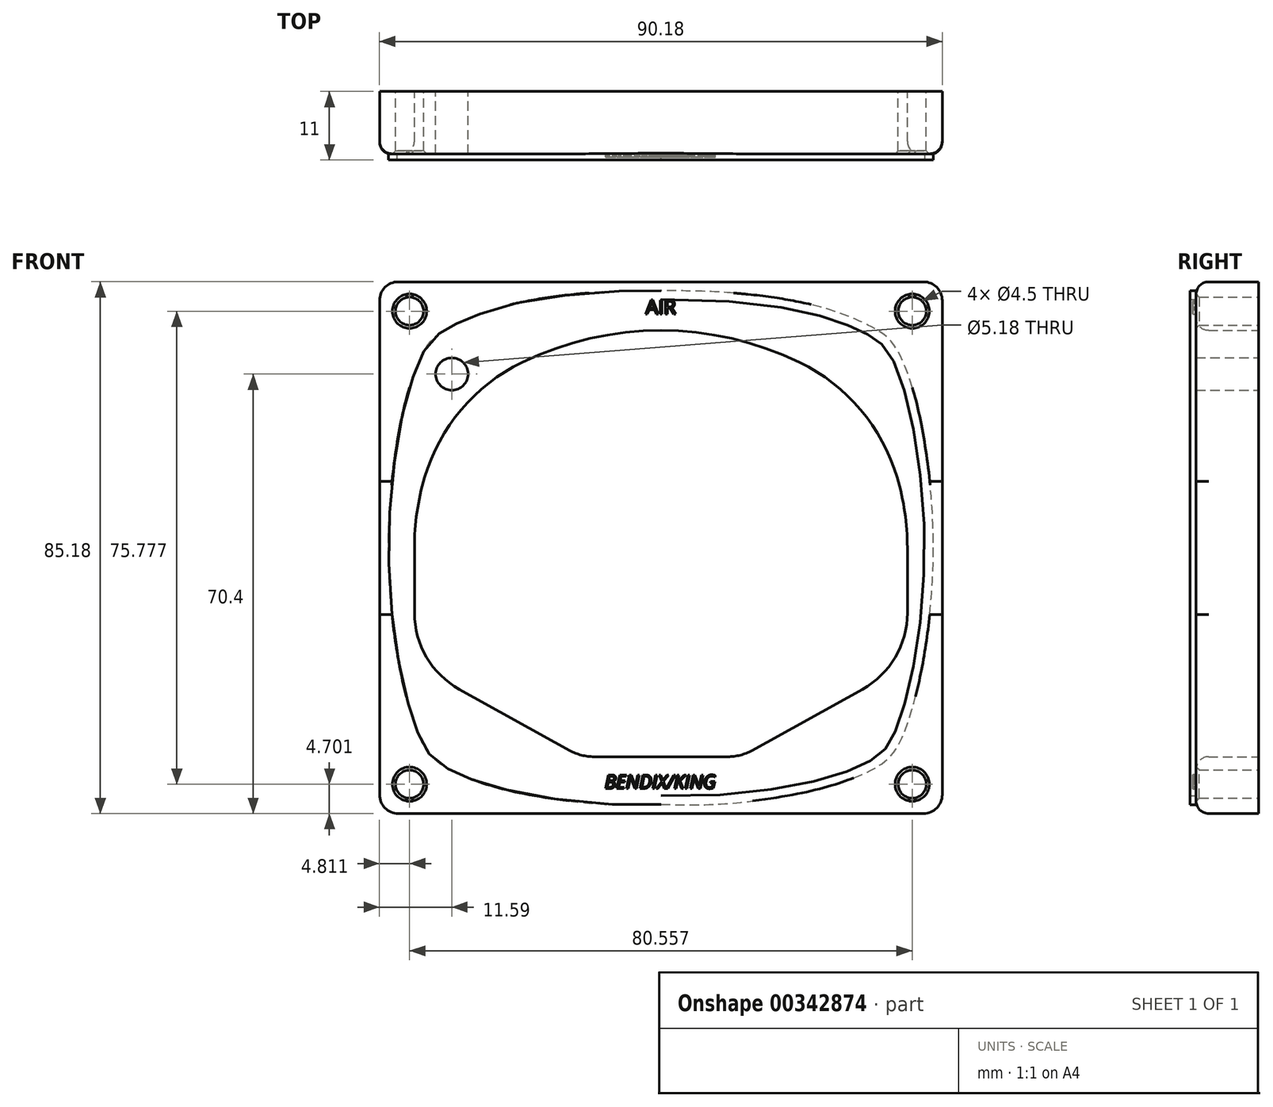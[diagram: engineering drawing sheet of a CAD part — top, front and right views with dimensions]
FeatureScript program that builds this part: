
annotation { "Feature Type Name" : "Feature", "Feature Type Description" : "" }
export const myFeature = defineFeature(function(context is Context, id is Id, definition is map)
    precondition{}
    {
        {
            var Q0;
            Q0=qCreatedBy(makeId("Front.planeOp"),FACE);
            var sketch = newSketch(context, id + "F0", { "sketchPlane" : qUnion([Q0])});
            skArc(sketch, "E0", {"start": v(0, 34.8) * mm, "mid": v(-11.41, 33.5) * mm, "end": v(-22.25, 29.67) * mm});
            skPoint(sketch, "E1.newPointA", {"position": v(39.5, 0) * mm});
            skPoint(sketch, "E1.newPointB", {"position": v(-48.21, 0) * mm});
            skArc(sketch, "E2", {"start": v(-39.5, 0) * mm, "mid": v(-39.1, 5.67) * mm, "end": v(-37.87, 11.23) * mm});
            skArc(sketch, "E3.filletArc", {"start": v(-22.25, 29.67) * mm, "mid": v(-32, 22.1) * mm, "end": v(-37.87, 11.23) * mm});
            skLineSegment(sketch, "E4", {"start": v(-10.73, -33.5) * mm, "end": v(0, -33.5) * mm});
            skLineSegment(sketch, "E5", {"start": v(-32.29, -22.7) * mm, "end": v(-14.6, -32.5) * mm});
            skLineSegment(sketch, "E6", {"start": v(-39.5, -10.45) * mm, "end": v(-39.5, 0) * mm});
            skPoint(sketch, "E7.visualSharp", {"position": v(-39.5, -18.7) * mm});
            skArc(sketch, "E7.filletArc", {"start": v(-39.5, -10.45) * mm, "mid": v(-37.56, -17.56) * mm, "end": v(-32.29, -22.7) * mm});
            skPoint(sketch, "E8.visualSharp", {"position": v(-12.8, -33.5) * mm});
            skArc(sketch, "E8.filletArc", {"start": v(-14.6, -32.5) * mm, "mid": v(-12.73, -33.25) * mm, "end": v(-10.73, -33.5) * mm});
            skLineSegment(sketch, "E9", {"start": v(0, 56.24) * mm, "end": v(0, -63.83) * mm});
            skPoint(sketch, "E10.orphan", {"position": v(17.62, -33.5) * mm});
            skLineSegment(sketch, "E11.MirrorCS", {"start": v(10.73, -33.5) * mm, "end": v(0, -33.5) * mm});
            skArc(sketch, "E12.MirrorCS", {"start": v(14.6, -32.5) * mm, "mid": v(12.73, -33.25) * mm, "end": v(10.73, -33.5) * mm});
            skLineSegment(sketch, "E13.MirrorCS", {"start": v(39.5, -10.45) * mm, "end": v(39.5, 0) * mm});
            skLineSegment(sketch, "E14.MirrorCS", {"start": v(32.29, -22.7) * mm, "end": v(14.6, -32.5) * mm});
            skArc(sketch, "E15.MirrorCS", {"start": v(39.5, -10.45) * mm, "mid": v(37.56, -17.56) * mm, "end": v(32.29, -22.7) * mm});
            skArc(sketch, "E16.MirrorCS", {"start": v(39.5, 0) * mm, "mid": v(39.1, 5.67) * mm, "end": v(37.87, 11.23) * mm});
            skArc(sketch, "E17.MirrorCS", {"start": v(22.25, 29.67) * mm, "mid": v(32, 22.1) * mm, "end": v(37.87, 11.23) * mm});
            skArc(sketch, "E18.MirrorCS", {"start": v(0, 34.8) * mm, "mid": v(11.41, 33.5) * mm, "end": v(22.25, 29.67) * mm});
            skLineSegment(sketch, "E19.bottom", {"start": v(42.09, 42.59) * mm, "end": v(-42.09, 42.59) * mm});
            skLineSegment(sketch, "E19.top", {"start": v(42.09, -42.59) * mm, "end": v(-42.09, -42.59) * mm});
            skLineSegment(sketch, "E19.left", {"start": v(45.09, 39.59) * mm, "end": v(45.09, -39.59) * mm});
            skLineSegment(sketch, "E19.right", {"start": v(-45.09, 39.59) * mm, "end": v(-45.09, -39.59) * mm});
            skPoint(sketch, "E20.visualSharp", {"position": v(-45.09, 42.59) * mm});
            skArc(sketch, "E20.filletArc", {"start": v(-42.09, 42.59) * mm, "mid": v(-44.2, 41.7) * mm, "end": v(-45.09, 39.59) * mm});
            skPoint(sketch, "E21.visualSharp", {"position": v(45.09, 42.59) * mm});
            skArc(sketch, "E21.filletArc", {"start": v(45.09, 39.59) * mm, "mid": v(44.2, 41.7) * mm, "end": v(42.09, 42.59) * mm});
            skPoint(sketch, "E22.visualSharp", {"position": v(-45.09, -42.59) * mm});
            skArc(sketch, "E22.filletArc", {"start": v(-45.09, -39.59) * mm, "mid": v(-44.2, -41.7) * mm, "end": v(-42.09, -42.59) * mm});
            skPoint(sketch, "E23.visualSharp", {"position": v(45.09, -42.59) * mm});
            skArc(sketch, "E23.filletArc", {"start": v(42.09, -42.59) * mm, "mid": v(44.2, -41.7) * mm, "end": v(45.09, -39.59) * mm});
            skLineSegment(sketch, "E24", {"start": v(0, 0) * mm, "end": v(-42.09, 39.59) * mm, "construction": true});
            skCircle(sketch, "E25", {"center": v(-40.28, 37.89) * mm, "radius": 2.25 * mm});
            skLineSegment(sketch, "E26.bottom", {"start": v(-40.28, 37.89) * mm, "end": v(40.28, 37.89) * mm, "construction": true});
            skLineSegment(sketch, "E26.top", {"start": v(-40.28, -37.89) * mm, "end": v(40.28, -37.89) * mm, "construction": true});
            skLineSegment(sketch, "E26.left", {"start": v(-40.28, 37.89) * mm, "end": v(-40.28, -37.89) * mm, "construction": true});
            skLineSegment(sketch, "E26.right", {"start": v(40.28, 37.89) * mm, "end": v(40.28, -37.89) * mm, "construction": true});
            skCircle(sketch, "E27.0.1.0", {"center": v(-40.28, -37.89) * mm, "radius": 2.25 * mm});
            skCircle(sketch, "E27.1.0.0", {"center": v(40.28, 37.89) * mm, "radius": 2.25 * mm});
            skCircle(sketch, "E27.1.1.0", {"center": v(40.28, -37.89) * mm, "radius": 2.25 * mm});
            skCircle(sketch, "E28", {"center": v(-33.5, 27.81) * mm, "radius": 2.59 * mm});
            skSolve(sketch);
        }
        {
            var Q0;
            {var subQ4=sQuery(id+"F0.wireOp",EDGE,"E0");Q0=makeQuery(id+"F0.imprint","IMPRINT",FACE,{"disambiguationData":[TD([[makeQuery(id+"F0.imprint","IMPRINT",EDGE,{"derivedFrom":subQ4}),-1.0]])]});}
            var Q1;
            {var subQ4=sQuery(id+"F0.wireOp",EDGE,"E11.MirrorCS");Q1=makeQuery(id+"F0.imprint","IMPRINT",FACE,{"disambiguationData":[TD([[makeQuery(id+"F0.imprint","IMPRINT",EDGE,{"derivedFrom":subQ4}),1.0]])]});}
            extrude(context, id + "F1", {"entities" : qUnion([Q0, Q1]), "depth" : 10 * mm});
        }
        {
            var Q0;
            Q0=makeQuery(id+"F1.opExtrude","CAP_FACE",FACE,{"disambiguationData":[OSD([sQuery(id+"F0.wireOp",EDGE,"E0"),sQuery(id+"F0.wireOp",EDGE,"E2"),sQuery(id+"F0.wireOp",EDGE,"E3.filletArc"),sQuery(id+"F0.wireOp",EDGE,"E4"),sQuery(id+"F0.wireOp",EDGE,"E5"),sQuery(id+"F0.wireOp",EDGE,"E6"),sQuery(id+"F0.wireOp",EDGE,"E7.filletArc"),sQuery(id+"F0.wireOp",EDGE,"E8.filletArc"),sQuery(id+"F0.wireOp",EDGE,"E11.MirrorCS"),sQuery(id+"F0.wireOp",EDGE,"E12.MirrorCS"),sQuery(id+"F0.wireOp",EDGE,"E13.MirrorCS"),sQuery(id+"F0.wireOp",EDGE,"E14.MirrorCS"),sQuery(id+"F0.wireOp",EDGE,"E15.MirrorCS"),sQuery(id+"F0.wireOp",EDGE,"E16.MirrorCS"),sQuery(id+"F0.wireOp",EDGE,"E17.MirrorCS"),sQuery(id+"F0.wireOp",EDGE,"E18.MirrorCS"),sQuery(id+"F0.wireOp",EDGE,"E19.bottom"),sQuery(id+"F0.wireOp",EDGE,"E19.top"),sQuery(id+"F0.wireOp",EDGE,"E19.left"),sQuery(id+"F0.wireOp",EDGE,"E19.right"),sQuery(id+"F0.wireOp",EDGE,"E20.filletArc"),sQuery(id+"F0.wireOp",EDGE,"E21.filletArc"),sQuery(id+"F0.wireOp",EDGE,"E22.filletArc"),sQuery(id+"F0.wireOp",EDGE,"E23.filletArc"),sQuery(id+"F0.wireOp",EDGE,"E25"),sQuery(id+"F0.wireOp",EDGE,"E27.0.1.0"),sQuery(id+"F0.wireOp",EDGE,"E27.1.0.0"),sQuery(id+"F0.wireOp",EDGE,"E27.1.1.0")])],"isStart":false});
            var sketch = newSketch(context, id + "F2", { "sketchPlane" : qUnion([Q0])});
            skPoint(sketch, "E29.centerSnap0", {"position": v(45.09, 0) * mm});
            skPoint(sketch, "E30.4.internal.snap0", {"position": v(0, -42.59) * mm});
            skFitSpline(sketch, "E30", {"points": [v(0, -39.77) * mm, v(-33.02, -34.46) * mm, v(-37.55, -29.49) * mm, v(-42.25, 0) * mm, v(-36.97, 30.45) * mm, v(-32.49, 34.5) * mm, v(0, 39.79) * mm], "startDerivative": vector(-232.92, -4.75) * mm, "endDerivative": vector(284.39, 0) * mm});
            skFitSpline(sketch, "E31.MirrorCS", {"points": [v(0, -39.77) * mm, v(33.02, -34.46) * mm, v(37.55, -29.49) * mm, v(42.25, 0) * mm, v(36.97, 30.45) * mm, v(32.49, 34.5) * mm, v(0, 39.79) * mm], "startDerivative": vector(232.92, -4.75) * mm, "endDerivative": vector(-284.39, 0) * mm});
            skFitSpline(sketch, "E32.0", {"points": [v(0.03, -41.11) * mm, v(-4.88, -41.21) * mm, v(-11.6, -40.92) * mm, v(-19.18, -39.93) * mm, v(-24.14, -38.96) * mm, v(-27.66, -38) * mm, v(-30.08, -37.2) * mm, v(-31.7, -36.57) * mm, v(-33.14, -35.92) * mm, v(-34.37, -35.28) * mm, v(-35.46, -34.59) * mm, v(-36.4, -33.8) * mm, v(-37.23, -32.87) * mm, v(-37.94, -31.82) * mm, v(-38.55, -30.61) * mm, v(-39.13, -29.23) * mm, v(-39.7, -27.63) * mm, v(-40.44, -25.23) * mm, v(-41.31, -21.77) * mm, v(-42.23, -17) * mm, v(-42.97, -11.74) * mm, v(-43.47, -6.13) * mm, v(-43.66, -0.3) * mm, v(-43.5, 5.58) * mm, v(-43, 11.35) * mm, v(-42.26, 16.83) * mm, v(-41.3, 21.85) * mm, v(-40.34, 25.5) * mm, v(-39.5, 28.01) * mm, v(-38.85, 29.69) * mm, v(-38.16, 31.14) * mm, v(-37.42, 32.34) * mm, v(-36.62, 33.34) * mm, v(-35.74, 34.15) * mm, v(-34.8, 34.8) * mm, v(-33.97, 35.27) * mm, v(-33.28, 35.61) * mm, v(-32.57, 35.96) * mm, v(-31.6, 36.4) * mm, v(-30.27, 36.96) * mm, v(-28.26, 37.71) * mm, v(-25.28, 38.64) * mm, v(-20.78, 39.64) * mm, v(-15.22, 40.45) * mm, v(-8.43, 41) * mm, v(-2.98, 41.14) * mm, v(0, 41.14) * mm]});
            skFitSpline(sketch, "E32.1", {"points": [v(-0.03, -41.11) * mm, v(4.88, -41.21) * mm, v(11.6, -40.92) * mm, v(19.18, -39.93) * mm, v(24.14, -38.96) * mm, v(27.66, -38) * mm, v(30.08, -37.2) * mm, v(31.7, -36.57) * mm, v(33.14, -35.92) * mm, v(34.37, -35.28) * mm, v(35.46, -34.59) * mm, v(36.4, -33.8) * mm, v(37.23, -32.87) * mm, v(37.94, -31.82) * mm, v(38.55, -30.61) * mm, v(39.13, -29.23) * mm, v(39.7, -27.63) * mm, v(40.44, -25.23) * mm, v(41.31, -21.77) * mm, v(42.23, -17) * mm, v(42.97, -11.74) * mm, v(43.47, -6.13) * mm, v(43.66, -0.3) * mm, v(43.5, 5.58) * mm, v(43, 11.35) * mm, v(42.26, 16.83) * mm, v(41.3, 21.85) * mm, v(40.34, 25.5) * mm, v(39.5, 28.01) * mm, v(38.85, 29.69) * mm, v(38.16, 31.14) * mm, v(37.42, 32.34) * mm, v(36.62, 33.34) * mm, v(35.74, 34.15) * mm, v(34.8, 34.8) * mm, v(33.97, 35.27) * mm, v(33.28, 35.61) * mm, v(32.57, 35.96) * mm, v(31.6, 36.4) * mm, v(30.27, 36.96) * mm, v(28.26, 37.71) * mm, v(25.28, 38.64) * mm, v(20.78, 39.64) * mm, v(15.22, 40.45) * mm, v(8.43, 41) * mm, v(2.98, 41.14) * mm, v(0, 41.14) * mm]});
            skText(sketch, "E33", { "text": "BENDIX/KING", "fontName": "OpenSans-Italic.ttf"});
            skText(sketch, "E34", { "text": "AIR", "fontName": "OpenSans-Regular.ttf"});
            const initialGuessF2  = {"E33": [-0.00901, -0.0386, 1, 0, 0.0022], "E34": [-0.00244, 0.0374, 1, 0, 0.00228]};
            skSetInitialGuess(sketch, initialGuessF2);
            skSolve(sketch);
        }
        {
            var Q0;
            Q0=makeQuery(id+"F2.imprint","IMPRINT",FACE,{"disambiguationData":[TD([[makeQuery(id+"F2.imprint","IMPRINT",EDGE,{"derivedFrom":sQuery(id+"F2.wireOp",EDGE,"E33.sketch_text.stroke-0")}),-1.0]])]});
            var Q1;
            Q1=makeQuery(id+"F2.imprint","IMPRINT",FACE,{"disambiguationData":[TD([[makeQuery(id+"F2.imprint","IMPRINT",EDGE,{"derivedFrom":sQuery(id+"F2.wireOp",EDGE,"E33.sketch_text.stroke-25")}),-1.0]])]});
            var Q2;
            Q2=makeQuery(id+"F2.imprint","IMPRINT",FACE,{"disambiguationData":[TD([[makeQuery(id+"F2.imprint","IMPRINT",EDGE,{"derivedFrom":sQuery(id+"F2.wireOp",EDGE,"E33.sketch_text.stroke-37")}),-1.0]])]});
            var Q3;
            Q3=makeQuery(id+"F2.imprint","IMPRINT",FACE,{"disambiguationData":[TD([[makeQuery(id+"F2.imprint","IMPRINT",EDGE,{"derivedFrom":sQuery(id+"F2.wireOp",EDGE,"E33.sketch_text.stroke-51")}),-1.0]])]});
            var Q4;
            Q4=makeQuery(id+"F2.imprint","IMPRINT",FACE,{"disambiguationData":[TD([[makeQuery(id+"F2.imprint","IMPRINT",EDGE,{"derivedFrom":sQuery(id+"F2.wireOp",EDGE,"E33.sketch_text.stroke-67")}),-1.0]])]});
            var Q5;
            Q5=makeQuery(id+"F2.imprint","IMPRINT",FACE,{"disambiguationData":[TD([[makeQuery(id+"F2.imprint","IMPRINT",EDGE,{"derivedFrom":sQuery(id+"F2.wireOp",EDGE,"E33.sketch_text.stroke-71")}),-1.0]])]});
            var Q6;
            Q6=makeQuery(id+"F2.imprint","IMPRINT",FACE,{"disambiguationData":[TD([[makeQuery(id+"F2.imprint","IMPRINT",EDGE,{"derivedFrom":sQuery(id+"F2.wireOp",EDGE,"E33.sketch_text.stroke-83")}),-1.0]])]});
            var Q7;
            Q7=makeQuery(id+"F2.imprint","IMPRINT",FACE,{"disambiguationData":[TD([[makeQuery(id+"F2.imprint","IMPRINT",EDGE,{"derivedFrom":sQuery(id+"F2.wireOp",EDGE,"E33.sketch_text.stroke-87")}),-1.0]])]});
            var Q8;
            Q8=makeQuery(id+"F2.imprint","IMPRINT",FACE,{"disambiguationData":[TD([[makeQuery(id+"F2.imprint","IMPRINT",EDGE,{"derivedFrom":sQuery(id+"F2.wireOp",EDGE,"E33.sketch_text.stroke-100")}),-1.0]])]});
            var Q9;
            Q9=makeQuery(id+"F2.imprint","IMPRINT",FACE,{"disambiguationData":[TD([[makeQuery(id+"F2.imprint","IMPRINT",EDGE,{"derivedFrom":sQuery(id+"F2.wireOp",EDGE,"E33.sketch_text.stroke-104")}),-1.0]])]});
            var Q10;
            Q10=makeQuery(id+"F2.imprint","IMPRINT",FACE,{"disambiguationData":[TD([[makeQuery(id+"F2.imprint","IMPRINT",EDGE,{"derivedFrom":sQuery(id+"F2.wireOp",EDGE,"E33.sketch_text.stroke-118")}),-1.0]])]});
            var Q11;
            Q11=makeQuery(id+"F2.imprint","IMPRINT",FACE,{"disambiguationData":[TD([[makeQuery(id+"F2.imprint","IMPRINT",EDGE,{"derivedFrom":sQuery(id+"F2.wireOp",EDGE,"E34.sketch_text.stroke-0")}),-1.0]])]});
            var Q12;
            Q12=makeQuery(id+"F2.imprint","IMPRINT",FACE,{"disambiguationData":[TD([[makeQuery(id+"F2.imprint","IMPRINT",EDGE,{"derivedFrom":sQuery(id+"F2.wireOp",EDGE,"E34.sketch_text.stroke-13")}),-1.0]])]});
            var Q13;
            Q13=makeQuery(id+"F2.imprint","IMPRINT",FACE,{"disambiguationData":[TD([[makeQuery(id+"F2.imprint","IMPRINT",EDGE,{"derivedFrom":sQuery(id+"F2.wireOp",EDGE,"E34.sketch_text.stroke-17")}),-1.0]])]});
            extrude(context, id + "F3", {"entities" : qUnion([Q0, Q1, Q2, Q3, Q4, Q5, Q6, Q7, Q8, Q9, Q10, Q11, Q12, Q13]), "operationType" : NewBodyOperationType.ADD, "depth" : 0.5 * mm});
        }
        {
            var Q0;
            Q0=makeQuery(id+"F2.imprint","IMPRINT",FACE,{"disambiguationData":[TD([[makeQuery(id+"F2.imprint","IMPRINT",EDGE,{"derivedFrom":sQuery(id+"F2.wireOp",EDGE,"E30")}),1.0]])]});
            extrude(context, id + "F4", {"entities" : qUnion([Q0]), "operationType" : NewBodyOperationType.ADD, "depth" : 1 * mm});
        }
        {
            var Q0;
            Q0=makeQuery(id+"F1.opExtrude","CAP_EDGE",EDGE,{"disambiguationData":[OSD([sQuery(id+"F0.wireOp",EDGE,"E19.bottom")])],"isStart":false});
            var Q1;
            Q1=makeQuery(id+"F1.opExtrude","CAP_EDGE",EDGE,{"disambiguationData":[OSD([sQuery(id+"F0.wireOp",EDGE,"E5")])],"isStart":false});
            fillet(context, id + "F5", {"entities" : qUnion([Q0, Q1]), "radius" : 2 * mm, "tangentPropagation" : true, "allowEdgeOverflow" : false});
        }
        {
            var Q0;
            Q0=makeQuery(id+"F1.opExtrude","CAP_EDGE",EDGE,{"disambiguationData":[OSD([sQuery(id+"F0.wireOp",EDGE,"E25")])],"isStart":false});
            var Q1;
            Q1=makeQuery(id+"F1.opExtrude","CAP_EDGE",EDGE,{"disambiguationData":[OSD([sQuery(id+"F0.wireOp",EDGE,"E27.1.0.0")])],"isStart":false});
            var Q2;
            Q2=makeQuery(id+"F1.opExtrude","CAP_EDGE",EDGE,{"disambiguationData":[OSD([sQuery(id+"F0.wireOp",EDGE,"E27.0.1.0")])],"isStart":false});
            var Q3;
            Q3=makeQuery(id+"F1.opExtrude","CAP_EDGE",EDGE,{"disambiguationData":[OSD([sQuery(id+"F0.wireOp",EDGE,"E27.1.1.0")])],"isStart":false});
            chamfer(context, id + "F6", {"entities" : qUnion([Q0, Q1, Q2, Q3]), "width" : 0.5 * mm, "tangentPropagation" : true});
        }
    });
